# Revit family: Class II Type A2 -677- Biological Safety Cabinet
name_source: partatom
category: Mechanical Equipment
revit_build: Autodesk Revit 2017 (Build: 20170419_0315(x64)
units: mm (PartAtom-declared; Revit-internal decimal feet)

## family parameters
Always vertical = Yes
Cut with Voids When Loaded = No
OmniClass Number = 23.75.00.00
OmniClass Title = Climate Control (HVAC)
Part Type = Normal
Room Calculation Point = No
Round Connector Dimension = Use Diameter
Shared = No
Work Plane-Based = No

## types (3) — shared parameters
DEPTH = 2' - 7 19/32"
Description = CLASS II TYPE A2 BIOLOGICAL SAFETY CABINET
HEIGHT = 4' - 10 7/8"
Manufacturer = Nuaire Inc. Plymouth MN USA
WORK SURFACE HEIGHT = 2' - 8 5/8"

## per-type parameters (varying)
| type | ACCESS HEIGHT | Clearance_Wall | LEG WIDTH | Model | WIDTH |
| 400 - 36" Work Surface Height | 0' - 8 9/32" | 0' - 8" | 4' - 1 13/16" | NU-677-400 | 4' - 5 13/16" |
| 500 - 36" Work Surface Height | 0' - 8 9/32" | 0' - 8" | 5' - 1 13/16" | NU-677-500 | 5' - 5 13/16" |
| 600 - 36" Work Surface Height | 1' - 0" | 0' - 6" | 6' - 1 13/16" | NU-677-600 | 6' - 5 13/16" |

## geometry (parser evidence)
native form markers: Blend x6, Sweep x2
no freeform markers — native parametric forms only
